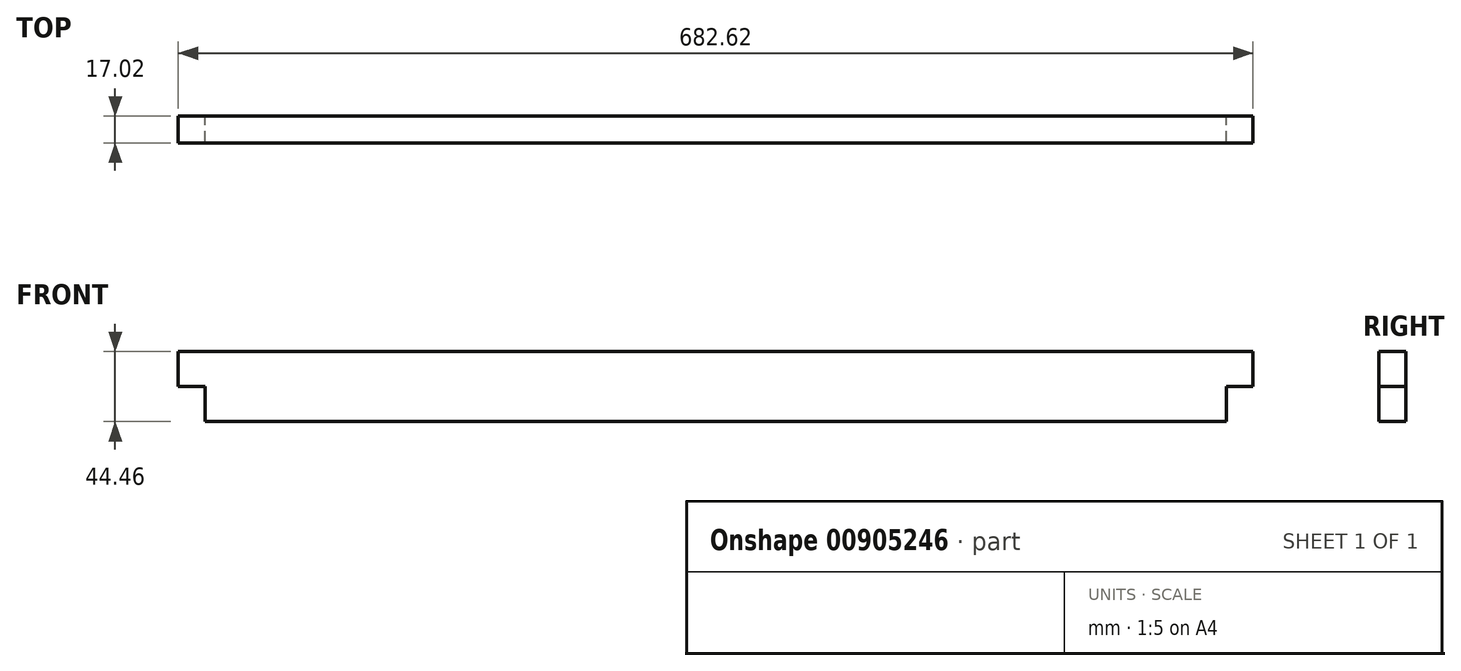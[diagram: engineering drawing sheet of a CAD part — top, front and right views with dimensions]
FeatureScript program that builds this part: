
annotation { "Feature Type Name" : "Feature", "Feature Type Description" : "" }
export const myFeature = defineFeature(function(context is Context, id is Id, definition is map)
    precondition{}
    {
        {
            var Q0;
            Q0=qCreatedBy(makeId("Front.planeOp"),FACE);
            var sketch = newSketch(context, id + "F0", { "sketchPlane" : qUnion([Q0])});
            skLineSegment(sketch, "E0.bottom", {"start": v(341.31, -22.23) * mm, "end": v(-341.31, -22.23) * mm});
            skLineSegment(sketch, "E0.top", {"start": v(341.31, 22.23) * mm, "end": v(-341.31, 22.22) * mm});
            skLineSegment(sketch, "E0.left", {"start": v(341.31, -22.23) * mm, "end": v(341.31, 22.22) * mm});
            skLineSegment(sketch, "E0.right", {"start": v(-341.31, -22.23) * mm, "end": v(-341.31, 22.22) * mm});
            skPoint(sketch, "E0.middle", {"position": v(0, 0) * mm});
            skSolve(sketch);
        }
        {
            var Q0;
            Q0=qSketchRegion(id+"F0",true);
            extrude(context, id + "F1", {"entities" : qUnion([Q0]), "offsetDistance" : 25.4 * mm, "depth" : 17.02 * mm});
        }
        {
            var Q0;
            Q0=makeQuery(id+"F0.imprint","IMPRINT",FACE,{"disambiguationData":[TD([[makeQuery(id+"F0.imprint","IMPRINT",EDGE,{"derivedFrom":sQuery(id+"F0.wireOp",EDGE,"E0.bottom")}),-1.0]])]});
            var sketch = newSketch(context, id + "F2", { "sketchPlane" : qUnion([Q0])});
            skLineSegment(sketch, "E1.bottom", {"start": v(-341.31, -22.23) * mm, "end": v(-324.3, -22.23) * mm});
            skLineSegment(sketch, "E1.top", {"start": v(-341.31, 0) * mm, "end": v(-324.3, 0) * mm});
            skLineSegment(sketch, "E1.left", {"start": v(-341.31, -22.23) * mm, "end": v(-341.31, 0) * mm});
            skLineSegment(sketch, "E1.right", {"start": v(-324.3, -22.23) * mm, "end": v(-324.3, 0) * mm});
            skLineSegment(sketch, "E2.MirrorCS", {"start": v(324.3, -22.23) * mm, "end": v(324.3, 0) * mm});
            skLineSegment(sketch, "E3.MirrorCS", {"start": v(341.31, -22.23) * mm, "end": v(341.31, 0) * mm});
            skLineSegment(sketch, "E4.MirrorCS", {"start": v(341.31, -22.23) * mm, "end": v(324.3, -22.23) * mm});
            skLineSegment(sketch, "E5.MirrorCS", {"start": v(341.31, 0) * mm, "end": v(324.3, 0) * mm});
            skSolve(sketch);
        }
        {
            var Q0;
            Q0=qSketchRegion(id+"F2",true);
            extrude(context, id + "F3", {"entities" : qUnion([Q0]), "operationType" : NewBodyOperationType.REMOVE, "endBound" : BoundingType.THROUGH_ALL, "depth" : 25.4 * mm});
        }
    });
